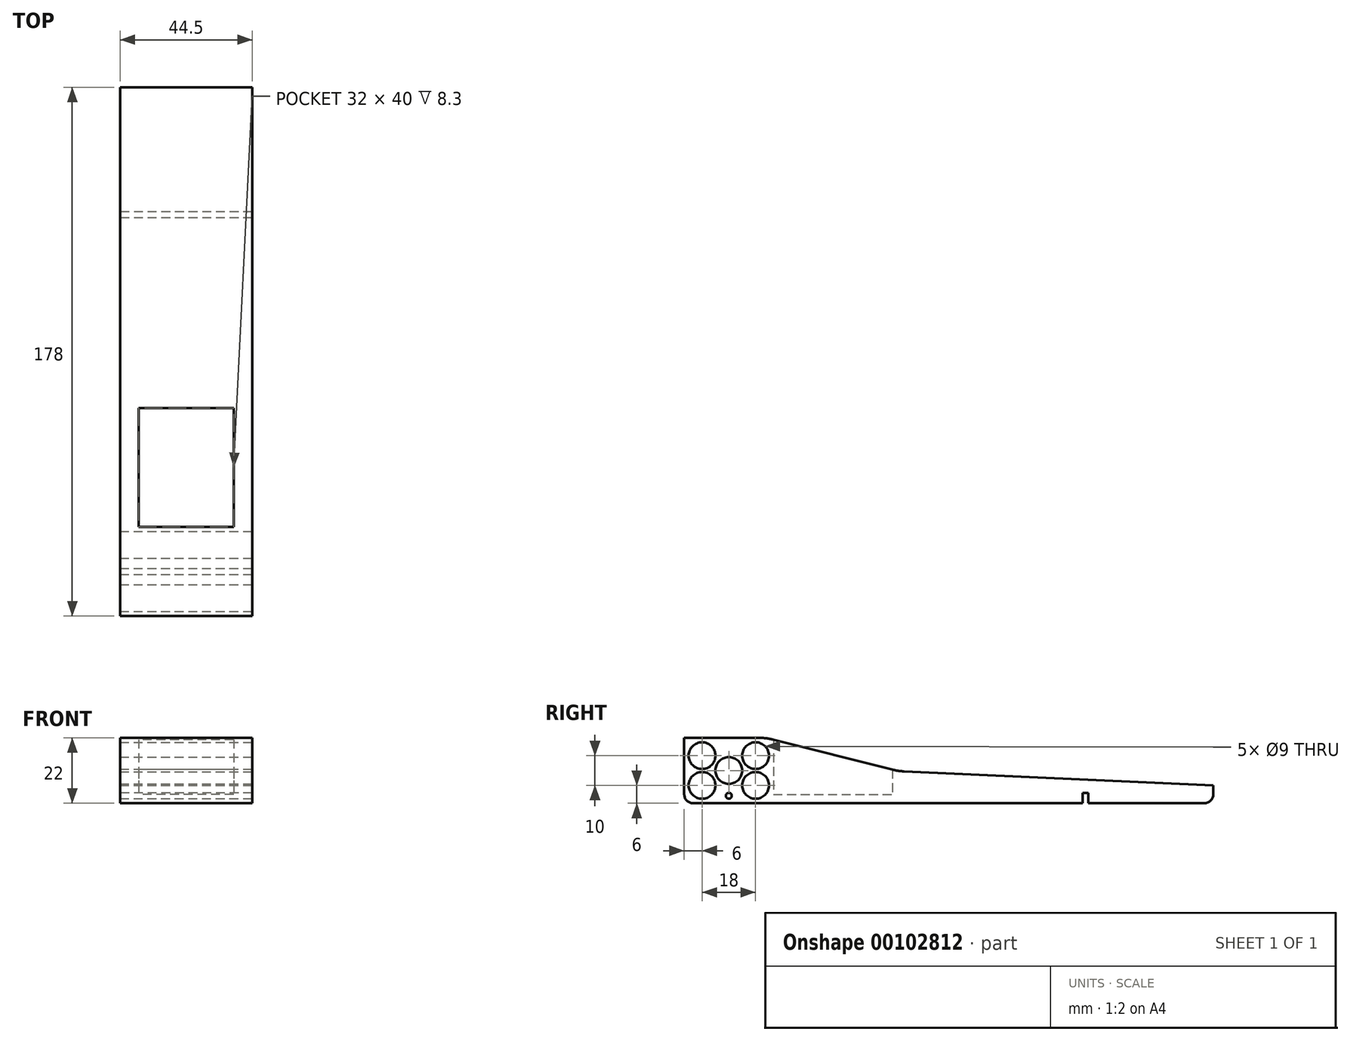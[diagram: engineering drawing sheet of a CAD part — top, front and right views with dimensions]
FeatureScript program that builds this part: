
annotation { "Feature Type Name" : "Feature", "Feature Type Description" : "" }
export const myFeature = defineFeature(function(context is Context, id is Id, definition is map)
    precondition{}
    {
        {
            var Q0;
            Q0=qCreatedBy(makeId("Right.planeOp"),FACE);
            var sketch = newSketch(context, id + "F0", { "sketchPlane" : qUnion([Q0])});
            skLineSegment(sketch, "E0.bottom", {"start": v(89, 16) * mm, "end": v(-89, 16) * mm});
            skLineSegment(sketch, "E0.top", {"start": v(89, -16) * mm, "end": v(-89, -16) * mm});
            skLineSegment(sketch, "E0.left", {"start": v(89, 16) * mm, "end": v(89, -16) * mm});
            skLineSegment(sketch, "E0.right", {"start": v(-89, 16) * mm, "end": v(-89, -16) * mm});
            skPoint(sketch, "E0.middle", {"position": v(0, 0) * mm});
            skLineSegment(sketch, "E1", {"start": v(45, -16) * mm, "end": v(45, -12.5) * mm});
            skLineSegment(sketch, "E2", {"start": v(45, -12.5) * mm, "end": v(47, -12.5) * mm});
            skLineSegment(sketch, "E3", {"start": v(47, -12.5) * mm, "end": v(47, -16) * mm});
            skLineSegment(sketch, "E4", {"start": v(-66, -16) * mm, "end": v(-66, -12.5) * mm});
            skLineSegment(sketch, "E5", {"start": v(-66, -12.5) * mm, "end": v(-64, -12.5) * mm});
            skLineSegment(sketch, "E6", {"start": v(-64, -12.5) * mm, "end": v(-64, -16) * mm});
            skSolve(sketch);
        }
        {
            var Q0;
            Q0=makeQuery(id+"F0.imprint","IMPRINT",FACE,{"disambiguationData":[TD([[makeQuery(id+"F0.imprint","IMPRINT",EDGE,{"derivedFrom":sQuery(id+"F0.wireOp",EDGE,"E0.bottom")}),1.0]])]});
            var Q1;
            {var subQ0=sQuery(id+"F0.wireOp",EDGE,"E4");Q1=makeQuery(id+"F0.imprint","IMPRINT",FACE,{"disambiguationData":[TD([[makeQuery(id+"F0.imprint","IMPRINT",EDGE,{"derivedFrom":subQ0}),-1.0]])]});}
            extrude(context, id + "F1", {"entities" : qUnion([Q0, Q1]), "depth" : 44.5 * mm, "symmetric" : true});
        }
        {
            var Q0;
            Q0=qCreatedBy(makeId("Right.planeOp"),FACE);
            var sketch = newSketch(context, id + "F2", { "sketchPlane" : qUnion([Q0])});
            skCircle(sketch, "E7", {"center": v(-74, -13.5) * mm, "radius": 1 * mm});
            skSolve(sketch);
        }
        {
            var Q0;
            Q0=qCreatedBy(makeId("Right.planeOp"),FACE);
            var sketch = newSketch(context, id + "F3", { "sketchPlane" : qUnion([Q0])});
            skCircle(sketch, "E8", {"center": v(-83, -10) * mm, "radius": 4.5 * mm});
            skCircle(sketch, "E9.1.0.0", {"center": v(-65, 0) * mm, "radius": 4.5 * mm});
            skLineSegment(sketch, "E10", {"start": v(-74, 16) * mm, "end": v(-74, -16) * mm, "construction": true});
            skPoint(sketch, "E11", {"position": v(-74, -13.5) * mm});
            skLineSegment(sketch, "E12.0", {"start": v(-48.6, 16) * mm, "end": v(-48.6, -16) * mm, "construction": true});
            skCircle(sketch, "E13.0.1.0", {"center": v(-83, 0) * mm, "radius": 4.5 * mm});
            skCircle(sketch, "E13.1.1.0", {"center": v(-74, -5) * mm, "radius": 4.5 * mm});
            skCircle(sketch, "E14", {"center": v(-65, -10) * mm, "radius": 4.5 * mm});
            skSolve(sketch);
        }
        {
            var Q0;
            Q0=qCreatedBy(makeId("Right.planeOp"),FACE);
            var sketch = newSketch(context, id + "F4", { "sketchPlane" : qUnion([Q0])});
            skLineSegment(sketch, "E15", {"start": v(-63.9, 6) * mm, "end": v(-89, 6) * mm});
            skLineSegment(sketch, "E16.0", {"start": v(-59, 5.4) * mm, "end": v(-59, -13) * mm});
            skLineSegment(sketch, "E17.0", {"start": v(-59, -13) * mm, "end": v(-19, -13) * mm});
            skLineSegment(sketch, "E18", {"start": v(-15.01, -5.29) * mm, "end": v(89, -10) * mm});
            skLineSegment(sketch, "E19", {"start": v(-59, 5.4) * mm, "end": v(-19, -4.7) * mm});
            skArc(sketch, "E20.filletArc", {"start": v(-59, 5.4) * mm, "mid": v(-61.43, 5.85) * mm, "end": v(-63.9, 6) * mm});
            skArc(sketch, "E21.filletArc", {"start": v(-19, -4.7) * mm, "mid": v(-17.02, -5.1) * mm, "end": v(-15.01, -5.29) * mm});
            skPoint(sketch, "E22", {"position": v(-74, -13.5) * mm});
            skLineSegment(sketch, "E23.0", {"start": v(-89, 16) * mm, "end": v(-89, -16) * mm});
            skLineSegment(sketch, "E24.0", {"start": v(89, 16) * mm, "end": v(-89, 16) * mm});
            skLineSegment(sketch, "E25.0", {"start": v(89, 16) * mm, "end": v(89, -16) * mm});
            skLineSegment(sketch, "E26", {"start": v(-19, -4.7) * mm, "end": v(-19, -13) * mm});
            skSolve(sketch);
        }
        {
            var Q0;
            Q0=makeQuery(id+"F2.imprint","IMPRINT",FACE,{"disambiguationData":[TD([[makeQuery(id+"F2.imprint","IMPRINT",EDGE,{"derivedFrom":sQuery(id+"F2.wireOp",EDGE,"E7")}),1.0]])]});
            extrude(context, id + "F5", {"entities" : qUnion([Q0]), "operationType" : NewBodyOperationType.REMOVE, "oppositeDirection" : true, "depth" : 50 * mm, "symmetric" : true});
        }
        {
            var Q0;
            Q0=makeQuery(id+"F3.imprint","IMPRINT",FACE,{"disambiguationData":[TD([[makeQuery(id+"F3.imprint","IMPRINT",EDGE,{"derivedFrom":sQuery(id+"F3.wireOp",EDGE,"E13.0.1.0")}),1.0]])]});
            var Q1;
            Q1=makeQuery(id+"F3.imprint","IMPRINT",FACE,{"disambiguationData":[TD([[makeQuery(id+"F3.imprint","IMPRINT",EDGE,{"derivedFrom":sQuery(id+"F3.wireOp",EDGE,"E8")}),1.0]])]});
            var Q2;
            Q2=makeQuery(id+"F3.imprint","IMPRINT",FACE,{"disambiguationData":[TD([[makeQuery(id+"F3.imprint","IMPRINT",EDGE,{"derivedFrom":sQuery(id+"F3.wireOp",EDGE,"E13.1.1.0")}),1.0]])]});
            var Q3;
            Q3=makeQuery(id+"F3.imprint","IMPRINT",FACE,{"disambiguationData":[TD([[makeQuery(id+"F3.imprint","IMPRINT",EDGE,{"derivedFrom":sQuery(id+"F3.wireOp",EDGE,"E9.1.0.0")}),1.0]])]});
            var Q4;
            Q4=makeQuery(id+"F3.imprint","IMPRINT",FACE,{"disambiguationData":[TD([[makeQuery(id+"F3.imprint","IMPRINT",EDGE,{"derivedFrom":sQuery(id+"F3.wireOp",EDGE,"E14")}),1.0]])]});
            extrude(context, id + "F6", {"entities" : qUnion([Q0, Q1, Q2, Q3, Q4]), "operationType" : NewBodyOperationType.REMOVE, "oppositeDirection" : true, "depth" : 50 * mm, "symmetric" : true});
        }
        {
            var Q0;
            {var subQ1=sQuery(id+"F4.wireOp",EDGE,"E15");Q0=makeQuery(id+"F4.imprint","IMPRINT",FACE,{"disambiguationData":[TD([[makeQuery(id+"F4.imprint","IMPRINT",EDGE,{"derivedFrom":subQ1}),-1.0]])]});}
            extrude(context, id + "F7", {"entities" : qUnion([Q0]), "operationType" : NewBodyOperationType.REMOVE, "oppositeDirection" : true, "depth" : 50 * mm, "symmetric" : true});
        }
        {
            var Q0;
            Q0=makeQuery(id+"F4.imprint","IMPRINT",FACE,{"disambiguationData":[TD([[makeQuery(id+"F4.imprint","IMPRINT",EDGE,{"derivedFrom":sQuery(id+"F4.wireOp",EDGE,"E16.0")}),1.0]])]});
            extrude(context, id + "F8", {"entities" : qUnion([Q0]), "operationType" : NewBodyOperationType.REMOVE, "depth" : 32 * mm, "symmetric" : true});
        }
        {
            var Q0;
            Q0=makeQuery(id+"F7.boolean.opBoolean","COPY",EDGE,{"derivedFrom":makeQuery(id+"F7.opExtrude","SWEPT_EDGE",EDGE,{"disambiguationData":[OSD([sQuery(id+"F4.wireOp",EDGE,"E18"),sQuery(id+"F4.wireOp",EDGE,"E25.0")])]})});
            var Q1;
            Q1=makeQuery(id+"F1.opExtrude","SWEPT_EDGE",EDGE,{"disambiguationData":[OSD([sQuery(id+"F0.wireOp",EDGE,"E0.top"),sQuery(id+"F0.wireOp",EDGE,"E0.left")])]});
            var Q2;
            Q2=makeQuery(id+"F7.boolean.opBoolean","COPY",EDGE,{"derivedFrom":makeQuery(id+"F7.opExtrude","SWEPT_EDGE",EDGE,{"disambiguationData":[OSD([sQuery(id+"F4.wireOp",EDGE,"E15"),sQuery(id+"F4.wireOp",EDGE,"E23.0")])]})});
            var Q3;
            Q3=makeQuery(id+"F1.opExtrude","SWEPT_EDGE",EDGE,{"disambiguationData":[OSD([sQuery(id+"F0.wireOp",EDGE,"E0.top"),sQuery(id+"F0.wireOp",EDGE,"E0.right")])]});
            fillet(context, id + "F9", {"entities" : qUnion([Q0, Q1, Q2, Q3]), "radius" : 3 * mm, "tangentPropagation" : true, "allowEdgeOverflow" : false});
        }
    });
